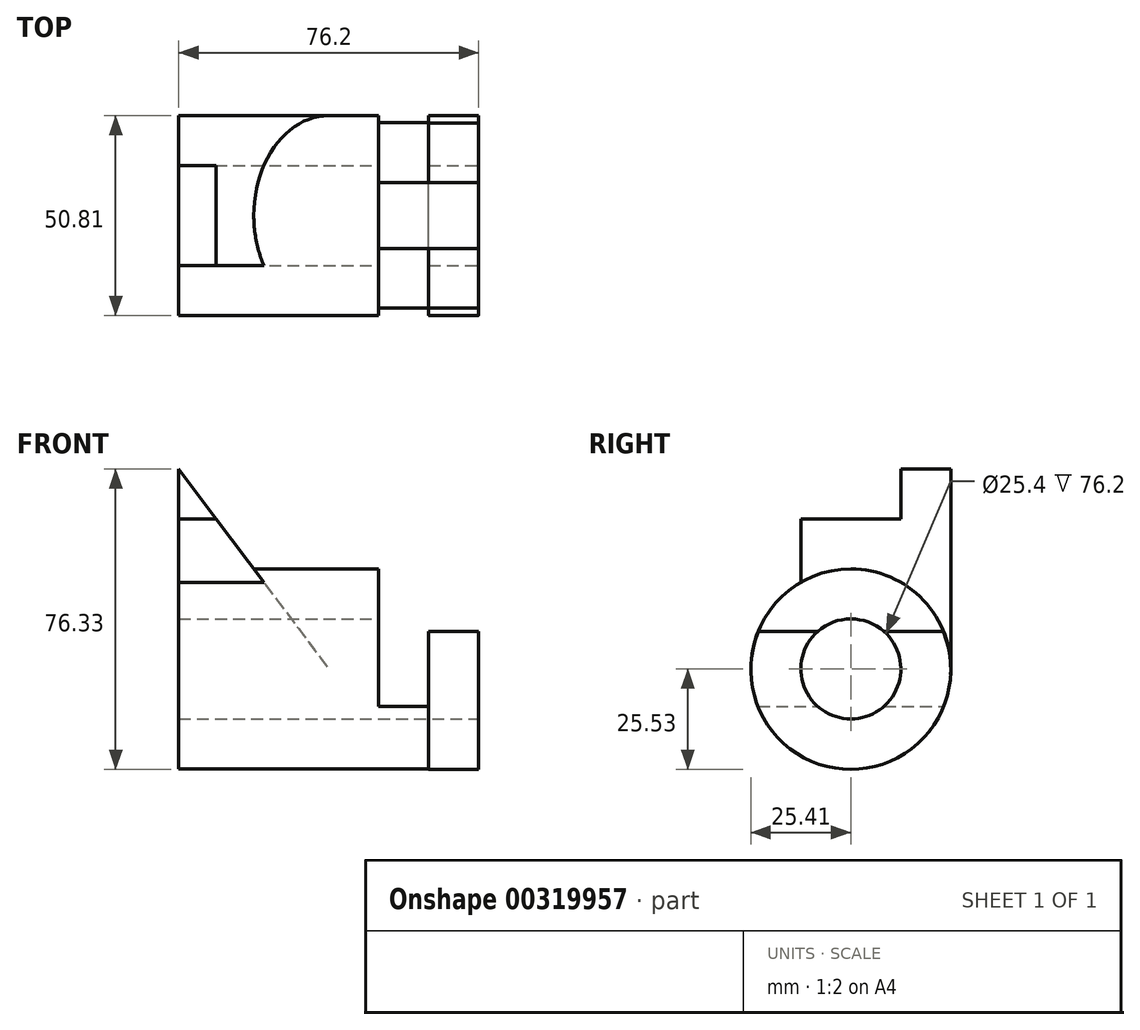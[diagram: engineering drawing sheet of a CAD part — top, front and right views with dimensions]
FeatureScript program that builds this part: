
annotation { "Feature Type Name" : "Feature", "Feature Type Description" : "" }
export const myFeature = defineFeature(function(context is Context, id is Id, definition is map)
    precondition{}
    {
        {
            var Q0;
            Q0=qCreatedBy(makeId("Right.planeOp"),FACE);
            var sketch = newSketch(context, id + "F0", { "sketchPlane" : qUnion([Q0])});
            skCircle(sketch, "E0", {"center": v(0, 0) * mm, "radius": 25.4 * mm});
            skSolve(sketch);
        }
        {
            var Q0;
            Q0 = qSketchRegion(id + "F0", true);
            extrude(context, id + "F1", {"entities" : qUnion([Q0]), "endBound" : BoundingType.SYMMETRIC, "depth" : 50.8 * mm});
        }
        {
            var Q0;
            Q0=makeQuery(id+"F1.opExtrude","CAP_FACE",FACE,{"disambiguationData":[OSD([sQuery(id+"F0.wireOp",EDGE,"E0")])],"isStart":false});
            var sketch = newSketch(context, id + "F2", { "sketchPlane" : qUnion([Q0])});
            skArc(sketch, "E1", {"start": v(-23.55, -9.53) * mm, "mid": v(0, -25.4) * mm, "end": v(23.55, -9.53) * mm});
            skLineSegment(sketch, "E2", {"start": v(-23.55, -9.52) * mm, "end": v(23.55, -9.53) * mm});
            skSolve(sketch);
        }
        {
            var Q0;
            Q0 = qSketchRegion(id + "F2", true);
            extrude(context, id + "F3", {"entities" : qUnion([Q0]), "operationType" : NewBodyOperationType.ADD, "depth" : 12.7 * mm});
        }
        {
            var Q0;
            Q0=makeQuery(id+"F3.opExtrude","CAP_FACE",FACE,{"disambiguationData":[OSD([sQuery(id+"F2.wireOp",EDGE,"E1"),sQuery(id+"F2.wireOp",EDGE,"E2")])],"isStart":false});
            var sketch = newSketch(context, id + "F4", { "sketchPlane" : qUnion([Q0])});
            skArc(sketch, "E3", {"start": v(-23.5, 9.52) * mm, "mid": v(0, -25.53) * mm, "end": v(23.49, 9.52) * mm});
            skLineSegment(sketch, "E4", {"start": v(-23.5, 9.52) * mm, "end": v(23.49, 9.52) * mm});
            skSolve(sketch);
        }
        {
            var Q0;
            Q0 = qSketchRegion(id + "F4", true);
            extrude(context, id + "F5", {"entities" : qUnion([Q0]), "operationType" : NewBodyOperationType.ADD, "depth" : 12.7 * mm});
        }
        {
            var Q0;
            Q0=qCreatedBy(makeId("Front.planeOp"),FACE);
            var sketch = newSketch(context, id + "F6", { "sketchPlane" : qUnion([Q0])});
            skLineSegment(sketch, "E5", {"start": v(0, 0) * mm, "end": v(-25.4, 0) * mm});
            skLineSegment(sketch, "E6", {"start": v(-25.4, 0) * mm, "end": v(12.7, 0) * mm});
            skLineSegment(sketch, "E7", {"start": v(-25.4, 0) * mm, "end": v(-25.4, 50.8) * mm});
            skLineSegment(sketch, "E8", {"start": v(-25.4, 50.8) * mm, "end": v(12.7, 0) * mm});
            skSolve(sketch);
        }
        {
            var Q0;
            Q0 = qSketchRegion(id + "F6", true);
            extrude(context, id + "F7", {"entities" : qUnion([Q0]), "operationType" : NewBodyOperationType.ADD, "oppositeDirection" : true, "depth" : 25.4 * mm});
        }
        {
            var Q0;
            Q0=makeQuery(id+"F7.opExtrude","CAP_FACE",FACE,{"disambiguationData":[OSD([sQuery(id+"F6.wireOp",EDGE,"E6"),sQuery(id+"F6.wireOp",EDGE,"E7"),sQuery(id+"F6.wireOp",EDGE,"E8")])],"isStart":true});
            var sketch = newSketch(context, id + "F8", { "sketchPlane" : qUnion([Q0])});
            skLineSegment(sketch, "E9", {"start": v(-25.4, 50.8) * mm, "end": v(-25.4, 0) * mm});
            skLineSegment(sketch, "E10", {"start": v(-25.4, 0) * mm, "end": v(12.7, 0) * mm});
            skLineSegment(sketch, "E11", {"start": v(12.7, 0) * mm, "end": v(-25.4, 50.8) * mm});
            skSolve(sketch);
        }
        {
            var Q0;
            Q0 = qSketchRegion(id + "F8", true);
            extrude(context, id + "F9", {"entities" : qUnion([Q0]), "operationType" : NewBodyOperationType.ADD, "depth" : 12.7 * mm});
        }
        {
            var Q0;
            Q0=makeQuery(id+"F5.opExtrude","CAP_FACE",FACE,{"disambiguationData":[OSD([sQuery(id+"F4.wireOp",EDGE,"E3"),sQuery(id+"F4.wireOp",EDGE,"E4")])],"isStart":false});
            var sketch = newSketch(context, id + "F10", { "sketchPlane" : qUnion([Q0])});
            skCircle(sketch, "E12", {"center": v(0, 0) * mm, "radius": 12.7 * mm});
            skSolve(sketch);
        }
        {
            var Q0;
            Q0 = qSketchRegion(id + "F10", true);
            extrude(context, id + "F11", {"entities" : qUnion([Q0]), "operationType" : NewBodyOperationType.REMOVE, "oppositeDirection" : true, "depth" : 76.2 * mm});
        }
        {
            var Q0;
            Q0=makeQuery(id+"F9.opExtrude","CAP_FACE",FACE,{"disambiguationData":[OSD([sQuery(id+"F8.wireOp",EDGE,"E9"),sQuery(id+"F8.wireOp",EDGE,"E10"),sQuery(id+"F8.wireOp",EDGE,"E11")])],"isStart":false});
            var sketch = newSketch(context, id + "F12", { "sketchPlane" : qUnion([Q0])});
            skLineSegment(sketch, "E13", {"start": v(-25.4, 50.8) * mm, "end": v(-25.4, 38.1) * mm});
            skLineSegment(sketch, "E14", {"start": v(-25.4, 38.1) * mm, "end": v(-15.87, 38.1) * mm});
            skLineSegment(sketch, "E15", {"start": v(-15.87, 38.1) * mm, "end": v(-25.4, 50.8) * mm});
            skSolve(sketch);
        }
        {
            var Q0;
            Q0 = qSketchRegion(id + "F12", true);
            extrude(context, id + "F13", {"entities" : qUnion([Q0]), "operationType" : NewBodyOperationType.REMOVE, "oppositeDirection" : true, "depth" : 25.4 * mm});
        }
    });
